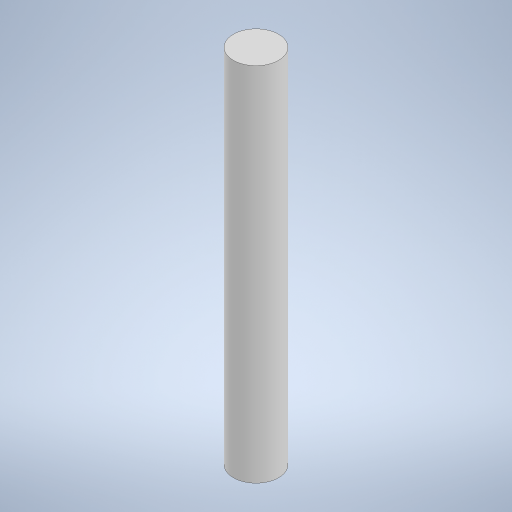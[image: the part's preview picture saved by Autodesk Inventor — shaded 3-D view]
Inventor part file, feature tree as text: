
AUTODESK INVENTOR PART (.ipt)
format: ipt  version: 2023 (Build 270158000, 158)  size: 222,208 bytes
history: native  units: mm
features: extrude x1, sketch x1
ambient origin geometry x8: Origin, YZ Plane, XZ Plane, XY Plane, X Axis, Y Axis, Z Axis, Center Point
bodies: Solid1 (feature_tree)
feature tree (2):
  extrude  "Extrusion1"  Depth=80.0mm TaperAngle=0.0deg
  sketch  "Sketch1"  dims[d0=10.0mm d1=80.0mm d2=0.0mm]
